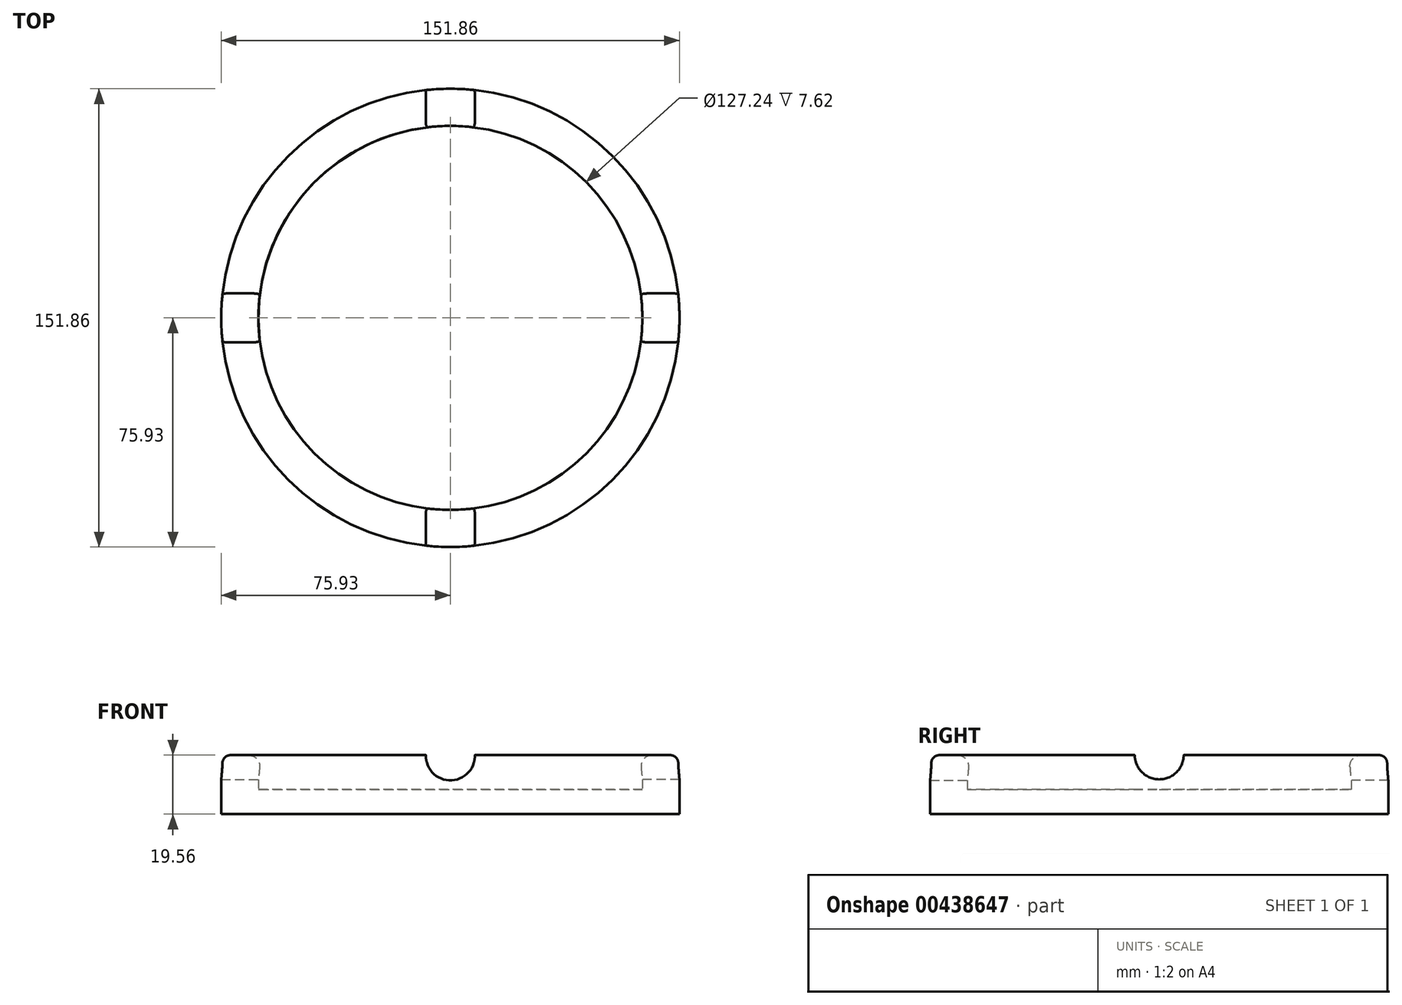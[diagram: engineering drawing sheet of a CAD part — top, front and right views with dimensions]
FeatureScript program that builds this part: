
annotation { "Feature Type Name" : "Feature", "Feature Type Description" : "" }
export const myFeature = defineFeature(function(context is Context, id is Id, definition is map)
    precondition{}
    {
        {
            var Q0;
            Q0=qCreatedBy(makeId("Top.planeOp"),FACE);
            var sketch = newSketch(context, id + "F0", { "sketchPlane" : qUnion([Q0])});
            skCircle(sketch, "E0", {"center": v(0, 0) * mm, "radius": 75.93 * mm});
            skCircle(sketch, "E1", {"center": v(0, 0) * mm, "radius": 63.62 * mm});
            skSolve(sketch);
        }
        {
            var Q0;
            Q0=makeQuery(id+"F0.imprint","IMPRINT",FACE,{"disambiguationData":[TD([[makeQuery(id+"F0.imprint","IMPRINT",EDGE,{"derivedFrom":sQuery(id+"F0.wireOp",EDGE,"E0")}),1.0]])]});
            var Q1;
            Q1=makeQuery(id+"F0.imprint","IMPRINT",FACE,{"disambiguationData":[TD([[makeQuery(id+"F0.imprint","IMPRINT",EDGE,{"derivedFrom":sQuery(id+"F0.wireOp",EDGE,"E1")}),1.0]])]});
            extrude(context, id + "F1", {"entities" : qUnion([Q0, Q1]), "oppositeDirection" : true, "depth" : 8.13 * mm});
        }
        {
            var Q0;
            Q0=makeQuery(id+"F0.imprint","IMPRINT",FACE,{"disambiguationData":[TD([[makeQuery(id+"F0.imprint","IMPRINT",EDGE,{"derivedFrom":sQuery(id+"F0.wireOp",EDGE,"E0")}),1.0]])]});
            extrude(context, id + "F2", {"entities" : qUnion([Q0]), "operationType" : NewBodyOperationType.ADD, "depth" : 11.43 * mm});
        }
        {
            var Q0;
            Q0=qCreatedBy(makeId("Right.planeOp"),FACE);
            var sketch = newSketch(context, id + "F3", { "sketchPlane" : qUnion([Q0])});
            skCircle(sketch, "E2", {"center": v(0, 11.51) * mm, "radius": 8.1 * mm});
            skSolve(sketch);
        }
        {
            var Q0;
            Q0=makeQuery(id+"F3.imprint","IMPRINT",FACE,{"disambiguationData":[TD([[makeQuery(id+"F3.imprint","IMPRINT",EDGE,{"derivedFrom":sQuery(id+"F3.wireOp",EDGE,"E2")}),1.0]])]});
            extrude(context, id + "F4", {"entities" : qUnion([Q0]), "operationType" : NewBodyOperationType.REMOVE, "oppositeDirection" : true, "depth" : 100.33 * mm});
        }
        {
            var Q0;
            Q0=makeQuery(id+"F3.imprint","IMPRINT",FACE,{"disambiguationData":[TD([[makeQuery(id+"F3.imprint","IMPRINT",EDGE,{"derivedFrom":sQuery(id+"F3.wireOp",EDGE,"E2")}),1.0]])]});
            extrude(context, id + "F5", {"entities" : qUnion([Q0]), "operationType" : NewBodyOperationType.REMOVE, "depth" : 117.1 * mm});
        }
        {
            var Q0;
            Q0=qCreatedBy(makeId("Front.planeOp"),FACE);
            var sketch = newSketch(context, id + "F6", { "sketchPlane" : qUnion([Q0])});
            skCircle(sketch, "E3", {"center": v(0, 11.18) * mm, "radius": 8.12 * mm});
            skSolve(sketch);
        }
        {
            var Q0;
            Q0=makeQuery(id+"F6.imprint","IMPRINT",FACE,{"disambiguationData":[TD([[makeQuery(id+"F6.imprint","IMPRINT",EDGE,{"derivedFrom":sQuery(id+"F6.wireOp",EDGE,"E3")}),1.0]])]});
            extrude(context, id + "F7", {"entities" : qUnion([Q0]), "operationType" : NewBodyOperationType.REMOVE, "oppositeDirection" : true, "depth" : 85.85 * mm});
        }
        {
            var Q0;
            Q0=makeQuery(id+"F6.imprint","IMPRINT",FACE,{"disambiguationData":[TD([[makeQuery(id+"F6.imprint","IMPRINT",EDGE,{"derivedFrom":sQuery(id+"F6.wireOp",EDGE,"E3")}),1.0]])]});
            extrude(context, id + "F8", {"entities" : qUnion([Q0]), "operationType" : NewBodyOperationType.REMOVE, "endBound" : BoundingType.SYMMETRIC, "depth" : 234.2 * mm});
        }
        {
            var Q0;
            {var subQ0=sQuery(id+"F0.wireOp",EDGE,"E0");Q0=makeQuery(id+"F7.boolean.opBoolean","SPLIT",EDGE,{"disambiguationData":[TD([makeQuery(id+"F4.boolean.opBoolean","COPY",FACE,{"derivedFrom":makeQuery(id+"F4.opExtrude","SWEPT_FACE",FACE,{"disambiguationData":[OSD([sQuery(id+"F3.wireOp",EDGE,"E2")])]})})])],"derivedFrom":makeQuery(id+"F5.boolean.opBoolean","SPLIT",EDGE,{"disambiguationData":[OD(1.0)],"derivedFrom":makeQuery(id+"F2.opExtrude","CAP_EDGE",EDGE,{"disambiguationData":[OSD([subQ0])],"isStart":false})})});}
            var Q1;
            {var subQ0=sQuery(id+"F0.wireOp",EDGE,"E0");Q1=makeQuery(id+"F7.boolean.opBoolean","SPLIT",EDGE,{"disambiguationData":[TD([makeQuery(id+"F5.boolean.opBoolean","COPY",FACE,{"derivedFrom":makeQuery(id+"F5.opExtrude","SWEPT_FACE",FACE,{"disambiguationData":[OSD([sQuery(id+"F3.wireOp",EDGE,"E2")])]})})])],"derivedFrom":makeQuery(id+"F5.boolean.opBoolean","SPLIT",EDGE,{"disambiguationData":[OD(1.0)],"derivedFrom":makeQuery(id+"F2.opExtrude","CAP_EDGE",EDGE,{"disambiguationData":[OSD([subQ0])],"isStart":false})})});}
            var Q2;
            {var subQ0=sQuery(id+"F0.wireOp",EDGE,"E0");Q2=makeQuery(id+"F8.boolean.opBoolean","SPLIT",EDGE,{"disambiguationData":[TD([makeQuery(id+"F4.boolean.opBoolean","COPY",FACE,{"derivedFrom":makeQuery(id+"F4.opExtrude","SWEPT_FACE",FACE,{"disambiguationData":[OSD([sQuery(id+"F3.wireOp",EDGE,"E2")])]})})])],"derivedFrom":makeQuery(id+"F5.boolean.opBoolean","SPLIT",EDGE,{"disambiguationData":[OD(0.0)],"derivedFrom":makeQuery(id+"F2.opExtrude","CAP_EDGE",EDGE,{"disambiguationData":[OSD([subQ0])],"isStart":false})})});}
            var Q3;
            {var subQ0=sQuery(id+"F0.wireOp",EDGE,"E0");Q3=makeQuery(id+"F8.boolean.opBoolean","SPLIT",EDGE,{"disambiguationData":[TD([makeQuery(id+"F5.boolean.opBoolean","COPY",FACE,{"derivedFrom":makeQuery(id+"F5.opExtrude","SWEPT_FACE",FACE,{"disambiguationData":[OSD([sQuery(id+"F3.wireOp",EDGE,"E2")])]})})])],"derivedFrom":makeQuery(id+"F5.boolean.opBoolean","SPLIT",EDGE,{"disambiguationData":[OD(0.0)],"derivedFrom":makeQuery(id+"F2.opExtrude","CAP_EDGE",EDGE,{"disambiguationData":[OSD([subQ0])],"isStart":false})})});}
            fillet(context, id + "F9", {"entities" : qUnion([Q0, Q1, Q2, Q3]), "radius" : 2.54 * mm, "tangentPropagation" : true, "allowEdgeOverflow" : false});
        }
        {
            var Q0;
            {var subQ0=sQuery(id+"F0.wireOp",EDGE,"E1");Q0=makeQuery(id+"F7.boolean.opBoolean","SPLIT",EDGE,{"disambiguationData":[TD([makeQuery(id+"F5.boolean.opBoolean","COPY",FACE,{"derivedFrom":makeQuery(id+"F5.opExtrude","SWEPT_FACE",FACE,{"disambiguationData":[OSD([sQuery(id+"F3.wireOp",EDGE,"E2")])]})})])],"derivedFrom":makeQuery(id+"F5.boolean.opBoolean","SPLIT",EDGE,{"disambiguationData":[OD(1.0)],"derivedFrom":makeQuery(id+"F2.opExtrude","CAP_EDGE",EDGE,{"disambiguationData":[OSD([subQ0])],"isStart":false})})});}
            var Q1;
            {var subQ0=sQuery(id+"F0.wireOp",EDGE,"E1");Q1=makeQuery(id+"F8.boolean.opBoolean","SPLIT",EDGE,{"disambiguationData":[TD([makeQuery(id+"F5.boolean.opBoolean","COPY",FACE,{"derivedFrom":makeQuery(id+"F5.opExtrude","SWEPT_FACE",FACE,{"disambiguationData":[OSD([sQuery(id+"F3.wireOp",EDGE,"E2")])]})})])],"derivedFrom":makeQuery(id+"F5.boolean.opBoolean","SPLIT",EDGE,{"disambiguationData":[OD(0.0)],"derivedFrom":makeQuery(id+"F2.opExtrude","CAP_EDGE",EDGE,{"disambiguationData":[OSD([subQ0])],"isStart":false})})});}
            var Q2;
            {var subQ0=sQuery(id+"F0.wireOp",EDGE,"E1");Q2=makeQuery(id+"F8.boolean.opBoolean","SPLIT",EDGE,{"disambiguationData":[TD([makeQuery(id+"F4.boolean.opBoolean","COPY",FACE,{"derivedFrom":makeQuery(id+"F4.opExtrude","SWEPT_FACE",FACE,{"disambiguationData":[OSD([sQuery(id+"F3.wireOp",EDGE,"E2")])]})})])],"derivedFrom":makeQuery(id+"F5.boolean.opBoolean","SPLIT",EDGE,{"disambiguationData":[OD(0.0)],"derivedFrom":makeQuery(id+"F2.opExtrude","CAP_EDGE",EDGE,{"disambiguationData":[OSD([subQ0])],"isStart":false})})});}
            var Q3;
            {var subQ0=sQuery(id+"F0.wireOp",EDGE,"E1");Q3=makeQuery(id+"F7.boolean.opBoolean","SPLIT",EDGE,{"disambiguationData":[TD([makeQuery(id+"F4.boolean.opBoolean","COPY",FACE,{"derivedFrom":makeQuery(id+"F4.opExtrude","SWEPT_FACE",FACE,{"disambiguationData":[OSD([sQuery(id+"F3.wireOp",EDGE,"E2")])]})})])],"derivedFrom":makeQuery(id+"F5.boolean.opBoolean","SPLIT",EDGE,{"disambiguationData":[OD(1.0)],"derivedFrom":makeQuery(id+"F2.opExtrude","CAP_EDGE",EDGE,{"disambiguationData":[OSD([subQ0])],"isStart":false})})});}
            fillet(context, id + "F10", {"entities" : qUnion([Q0, Q1, Q2, Q3]), "radius" : 3.8 * mm, "tangentPropagation" : true, "allowEdgeOverflow" : false});
        }
    });
